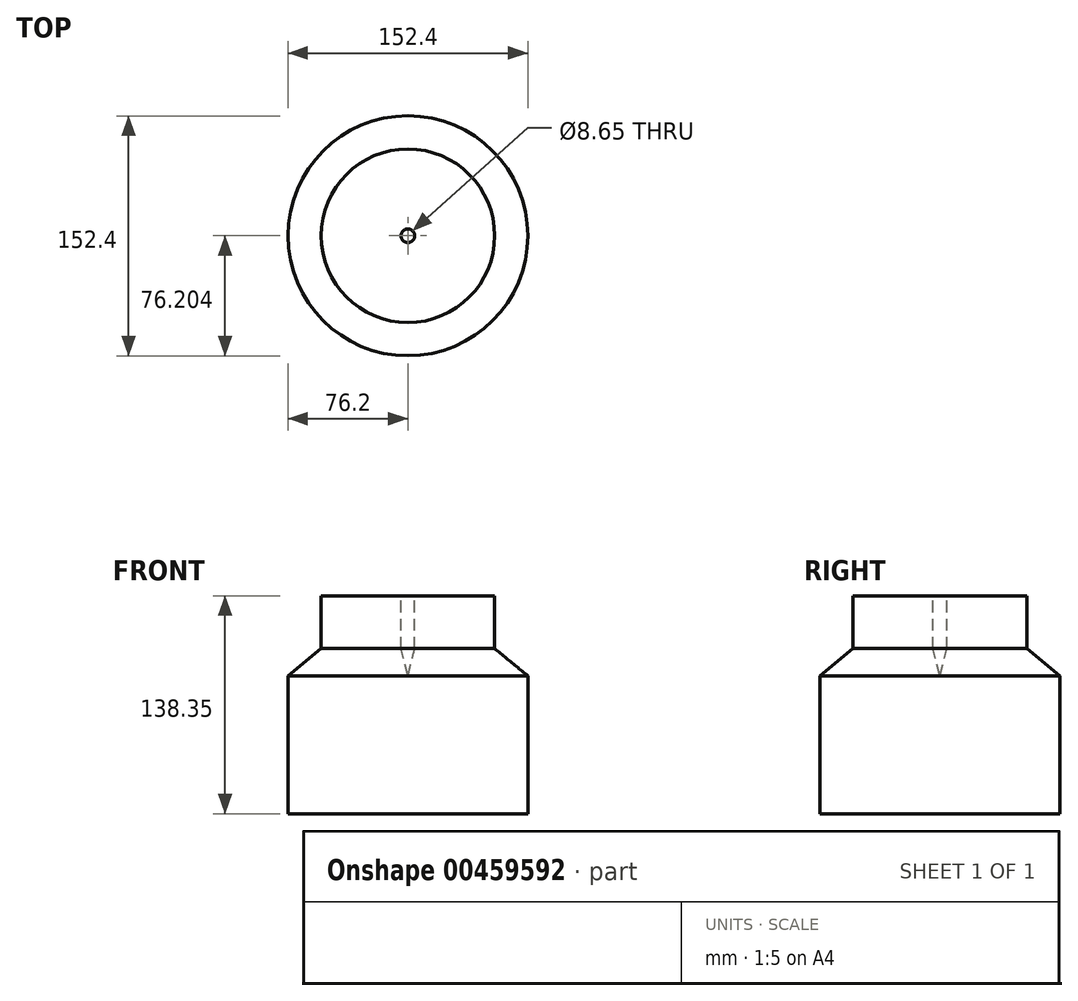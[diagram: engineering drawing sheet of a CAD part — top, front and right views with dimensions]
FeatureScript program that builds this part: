
annotation { "Feature Type Name" : "Feature", "Feature Type Description" : "" }
export const myFeature = defineFeature(function(context is Context, id is Id, definition is map)
    precondition{}
    {
        {
            var Q0;
            Q0=qCreatedBy(makeId("Right.planeOp"),FACE);
            var sketch = newSketch(context, id + "F0", { "sketchPlane" : qUnion([Q0])});
            skLineSegment(sketch, "E0.bottom", {"start": v(-36.7, 38.1) * mm, "end": v(39.5, 38.1) * mm});
            skLineSegment(sketch, "E0.top", {"start": v(-36.7, -49.45) * mm, "end": v(39.5, -49.45) * mm});
            skLineSegment(sketch, "E0.left", {"start": v(-36.7, 38.1) * mm, "end": v(-36.7, -49.45) * mm});
            skLineSegment(sketch, "E0.right", {"start": v(39.5, 38.1) * mm, "end": v(39.5, -49.45) * mm});
            skLineSegment(sketch, "E1.bottom", {"start": v(-32.37, 88.9) * mm, "end": v(18.43, 88.9) * mm});
            skLineSegment(sketch, "E1.top", {"start": v(-32.37, 55.4) * mm, "end": v(18.43, 55.4) * mm});
            skLineSegment(sketch, "E1.left", {"start": v(-32.37, 88.9) * mm, "end": v(-32.37, 55.4) * mm});
            skLineSegment(sketch, "E1.right", {"start": v(18.43, 88.9) * mm, "end": v(18.43, 55.4) * mm});
            skLineSegment(sketch, "E2", {"start": v(-32.37, 55.4) * mm, "end": v(-36.7, 38.1) * mm});
            skLineSegment(sketch, "E3", {"start": v(18.43, 55.4) * mm, "end": v(39.5, 38.1) * mm});
            skSolve(sketch);
        }
        {
            var Q0;
            Q0=makeQuery(id+"F0.imprint","IMPRINT",FACE,{"disambiguationData":[TD([[makeQuery(id+"F0.imprint","IMPRINT",EDGE,{"derivedFrom":sQuery(id+"F0.wireOp",EDGE,"E1.bottom")}),-1.0]])]});
            var Q1;
            Q1=makeQuery(id+"F0.imprint","IMPRINT",FACE,{"disambiguationData":[TD([[makeQuery(id+"F0.imprint","IMPRINT",EDGE,{"derivedFrom":sQuery(id+"F0.wireOp",EDGE,"E0.bottom")}),-1.0]])]});
            var Q2;
            Q2=makeQuery(id+"F0.imprint","IMPRINT",FACE,{"disambiguationData":[TD([[makeQuery(id+"F0.imprint","IMPRINT",EDGE,{"derivedFrom":sQuery(id+"F0.wireOp",EDGE,"E0.bottom")}),1.0]])]});
            var Q3;
            Q3=sQuery(id+"F0.wireOp",EDGE,"E0.left");
            revolve(context, id + "F1", {"entities" : qUnion([Q0, Q1, Q2]), "axis" : qUnion([Q3]), "revolveType" : RevolveType.FULL});
        }
    });
